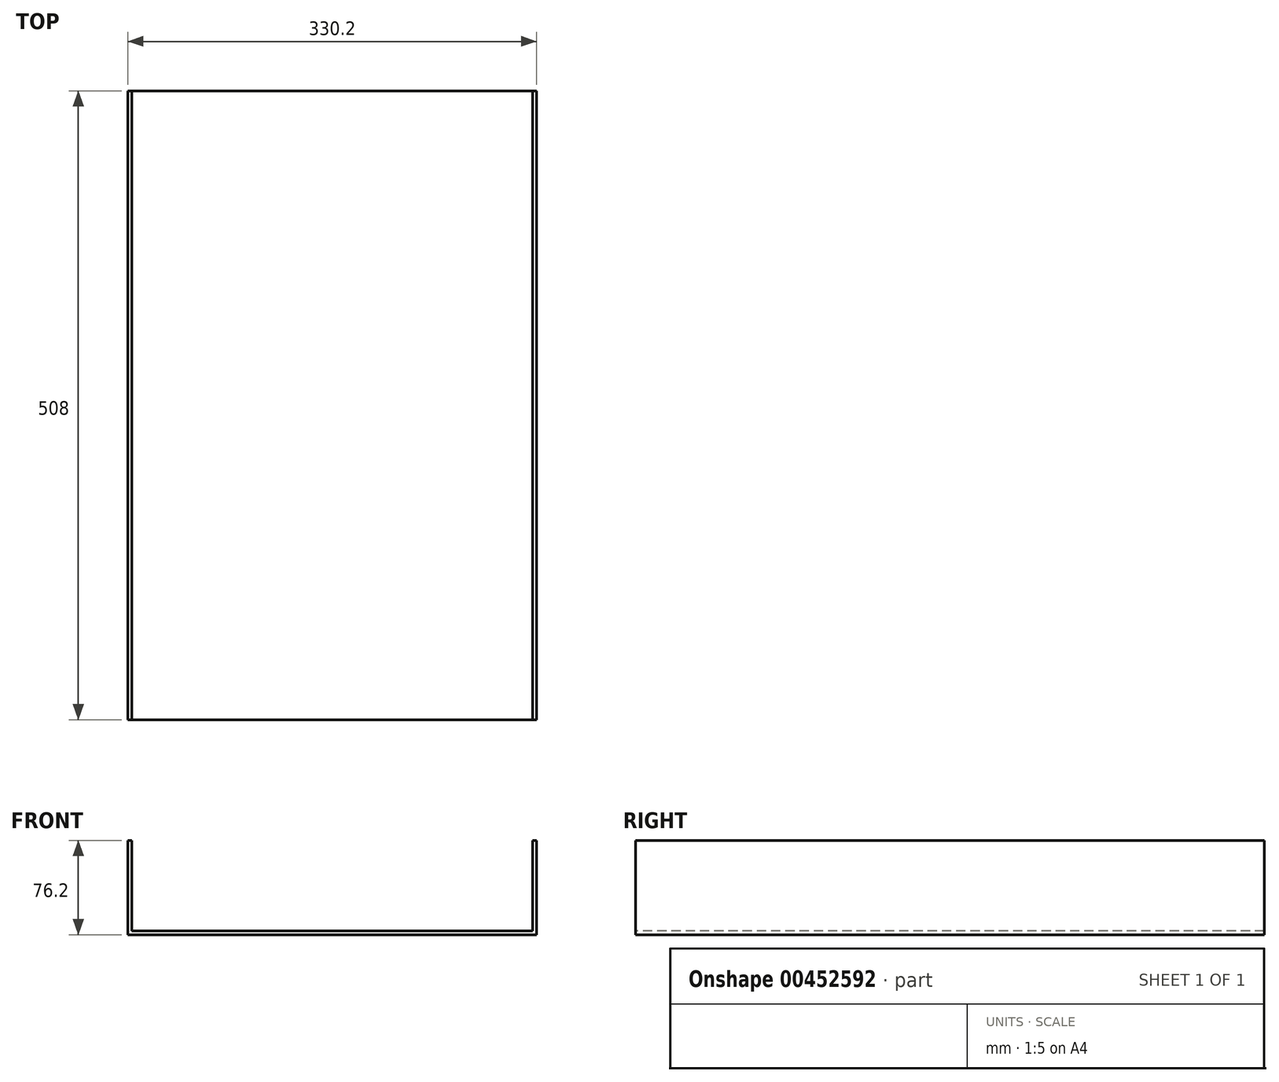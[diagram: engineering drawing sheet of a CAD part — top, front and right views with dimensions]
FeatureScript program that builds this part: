
annotation { "Feature Type Name" : "Feature", "Feature Type Description" : "" }
export const myFeature = defineFeature(function(context is Context, id is Id, definition is map)
    precondition{}
    {
        {
            var Q0;
            Q0=qCreatedBy(makeId("Top.planeOp"),FACE);
            var sketch = newSketch(context, id + "F0", { "sketchPlane" : qUnion([Q0])});
            skLineSegment(sketch, "E0.bottom", {"start": v(165.1, 254) * mm, "end": v(-165.1, 254) * mm});
            skLineSegment(sketch, "E0.top", {"start": v(165.1, -254) * mm, "end": v(-165.1, -254) * mm});
            skLineSegment(sketch, "E0.left", {"start": v(165.1, 254) * mm, "end": v(165.1, -254) * mm});
            skLineSegment(sketch, "E0.right", {"start": v(-165.1, 254) * mm, "end": v(-165.1, -254) * mm});
            skPoint(sketch, "E0.middle", {"position": v(0, 0) * mm});
            skSolve(sketch);
        }
        {
            var Q0;
            Q0=qSketchRegion(id+"F0",true);
            extrude(context, id + "F1", {"entities" : qUnion([Q0]), "depth" : 76.2 * mm});
        }
        {
            var Q0;
            Q0=makeQuery(id+"F1.opExtrude","CAP_FACE",FACE,{"disambiguationData":[OSD([sQuery(id+"F0.wireOp",EDGE,"E0.bottom"),sQuery(id+"F0.wireOp",EDGE,"E0.top"),sQuery(id+"F0.wireOp",EDGE,"E0.left"),sQuery(id+"F0.wireOp",EDGE,"E0.right")])],"isStart":false});
            var Q1;
            Q1=makeQuery(id+"F1.opExtrude","SWEPT_FACE",FACE,{"disambiguationData":[OSD([sQuery(id+"F0.wireOp",EDGE,"E0.top")])]});
            var Q2;
            Q2=makeQuery(id+"F1.opExtrude","SWEPT_FACE",FACE,{"disambiguationData":[OSD([sQuery(id+"F0.wireOp",EDGE,"E0.bottom")])]});
            shell(context, id + "F2", {"entities" : qUnion([Q0, Q1, Q2]), "thickness" : 3.17 * mm});
        }
    });
